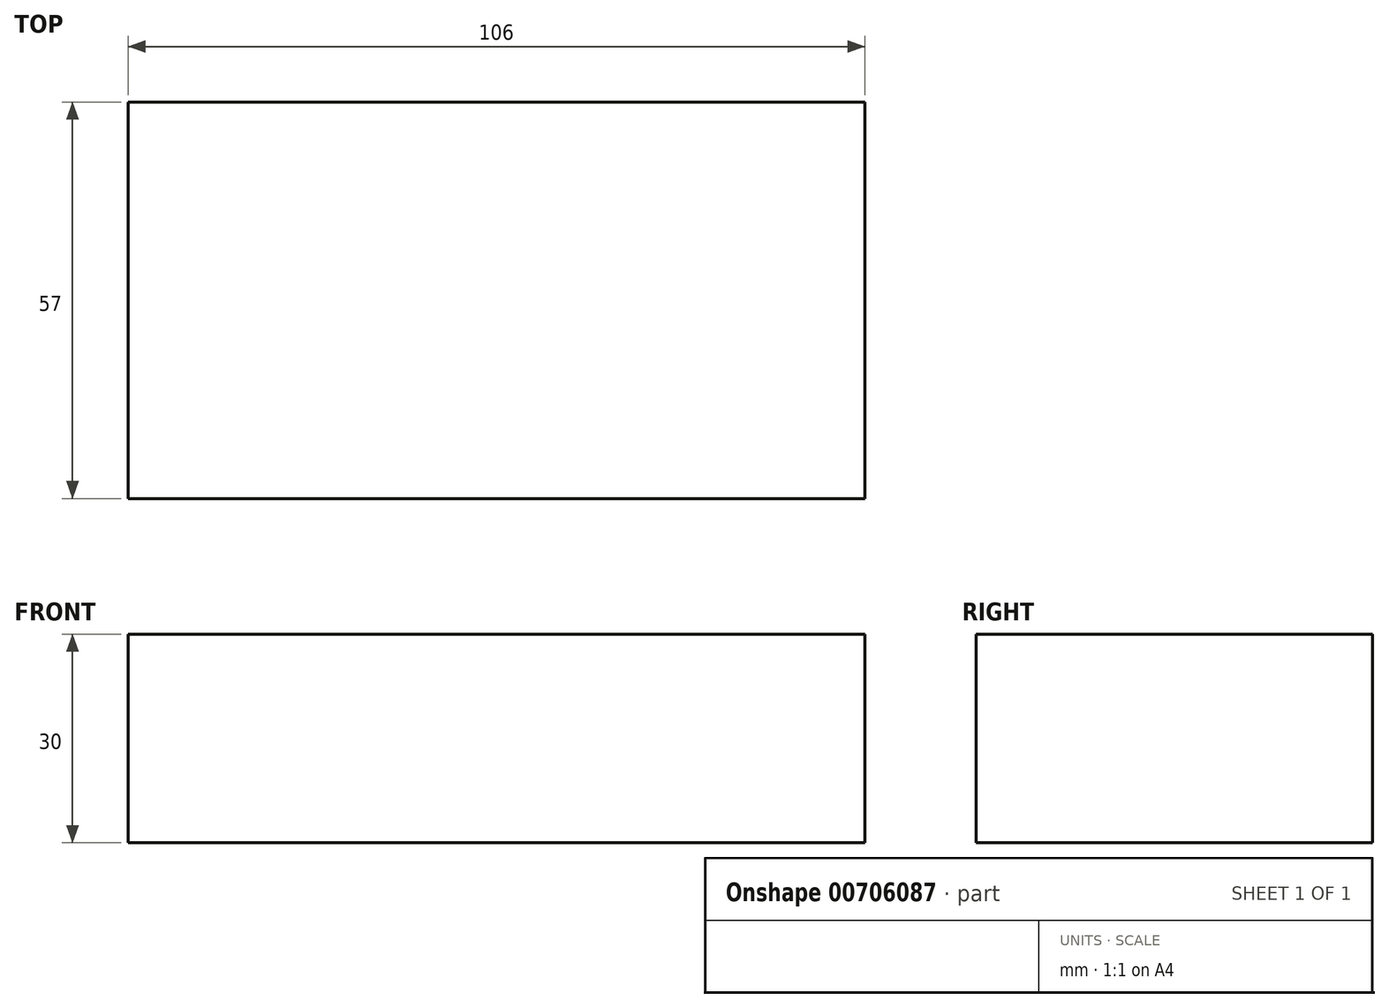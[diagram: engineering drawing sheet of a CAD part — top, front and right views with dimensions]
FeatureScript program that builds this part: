
annotation { "Feature Type Name" : "Feature", "Feature Type Description" : "" }
export const myFeature = defineFeature(function(context is Context, id is Id, definition is map)
    precondition{}
    {
        {
            var Q0;
            Q0=qCreatedBy(makeId("Top.planeOp"),FACE);
            var sketch = newSketch(context, id + "F0", { "sketchPlane" : qUnion([Q0])});
            skLineSegment(sketch, "E0.bottom", {"start": v(-53, -28.5) * mm, "end": v(53, -28.5) * mm});
            skLineSegment(sketch, "E0.top", {"start": v(-53, 28.5) * mm, "end": v(53, 28.5) * mm});
            skLineSegment(sketch, "E0.left", {"start": v(-53, -28.5) * mm, "end": v(-53, 28.5) * mm});
            skLineSegment(sketch, "E0.right", {"start": v(53, -28.5) * mm, "end": v(53, 28.5) * mm});
            skPoint(sketch, "E0.middle", {"position": v(0, 0) * mm});
            skSolve(sketch);
        }
        {
            var Q0;
            Q0=makeQuery(id+"F0.imprint","IMPRINT",FACE,{"disambiguationData":[TD([[makeQuery(id+"F0.imprint","IMPRINT",EDGE,{"derivedFrom":sQuery(id+"F0.wireOp",EDGE,"E0.bottom")}),1.0]])]});
            extrude(context, id + "F1", {"entities" : qUnion([Q0]), "depth" : 30 * mm, "offsetDistance" : 25.4 * mm});
        }
    });
